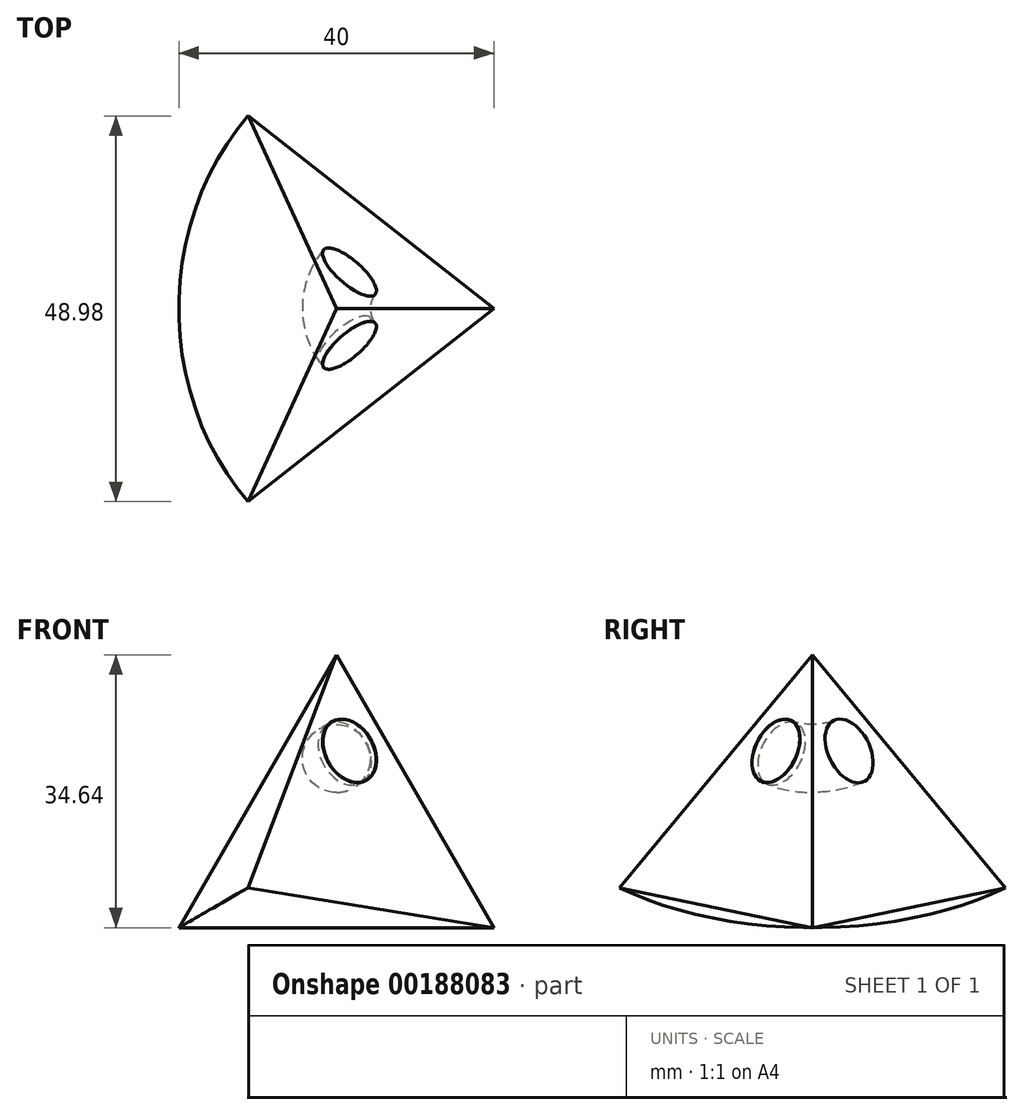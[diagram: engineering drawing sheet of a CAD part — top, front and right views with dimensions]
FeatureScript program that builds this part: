
annotation { "Feature Type Name" : "Feature", "Feature Type Description" : "" }
export const myFeature = defineFeature(function(context is Context, id is Id, definition is map)
    precondition{}
    {
        {
            var Q0;
            Q0=qCreatedBy(makeId("Front.planeOp"),FACE);
            var sketch = newSketch(context, id + "F0", { "sketchPlane" : qUnion([Q0])});
            skLineSegment(sketch, "E0", {"start": v(20, 0) * mm, "end": v(0, 0) * mm});
            skLineSegment(sketch, "E1", {"start": v(0, 0) * mm, "end": v(-20, 0) * mm});
            skLineSegment(sketch, "E2", {"start": v(-20, 0) * mm, "end": v(0, 0) * mm});
            skLineSegment(sketch, "E3", {"start": v(-20, 0) * mm, "end": v(0, 34.64) * mm});
            skLineSegment(sketch, "E4", {"start": v(0, 34.64) * mm, "end": v(20, 0) * mm});
            skCircle(sketch, "E5", {"center": v(0, 21.5) * mm, "radius": 4.32 * mm});
            skSolve(sketch);
        }
        {
            var Q0;
            Q0=makeQuery(id+"F0.imprint","IMPRINT",FACE,{"disambiguationData":[TD([[makeQuery(id+"F0.imprint","IMPRINT",EDGE,{"derivedFrom":sQuery(id+"F0.wireOp",EDGE,"E0")}),-1.0]])]});
            var Q1;
            Q1=sQuery(id+"F0.wireOp",EDGE,"E4");
            revolve(context, id + "F1", {"entities" : qUnion([Q0]), "axis" : qUnion([Q1]), "revolveType" : RevolveType.SYMMETRIC, "angle" : 90 * degree});
        }
        {
            var Q0;
            Q0=makeQuery(id+"F1.opRevolve","CAP_FACE",FACE,{"disambiguationData":[OSD([sQuery(id+"F0.wireOp",EDGE,"E0"),sQuery(id+"F0.wireOp",EDGE,"E2"),sQuery(id+"F0.wireOp",EDGE,"E3"),sQuery(id+"F0.wireOp",EDGE,"E4"),sQuery(id+"F0.wireOp",EDGE,"E5")])],"isStart":true});
            var sketch = newSketch(context, id + "F2", { "sketchPlane" : qUnion([Q0])});
            skCircle(sketch, "E6", {"center": v(-7.38, 18) * mm, "radius": 4.28 * mm});
            skSolve(sketch);
        }
        {
            var Q0;
            Q0=makeQuery(id+"F2.imprint","IMPRINT",FACE,{"disambiguationData":[TD([[makeQuery(id+"F2.imprint","IMPRINT",EDGE,{"derivedFrom":sQuery(id+"F2.wireOp",EDGE,"E6")}),1.0]])]});
            extrude(context, id + "F3", {"entities" : qUnion([Q0]), "oppositeDirection" : true, "depth" : 1 * mm, "offsetDistance" : 25 * mm});
        }
    });
